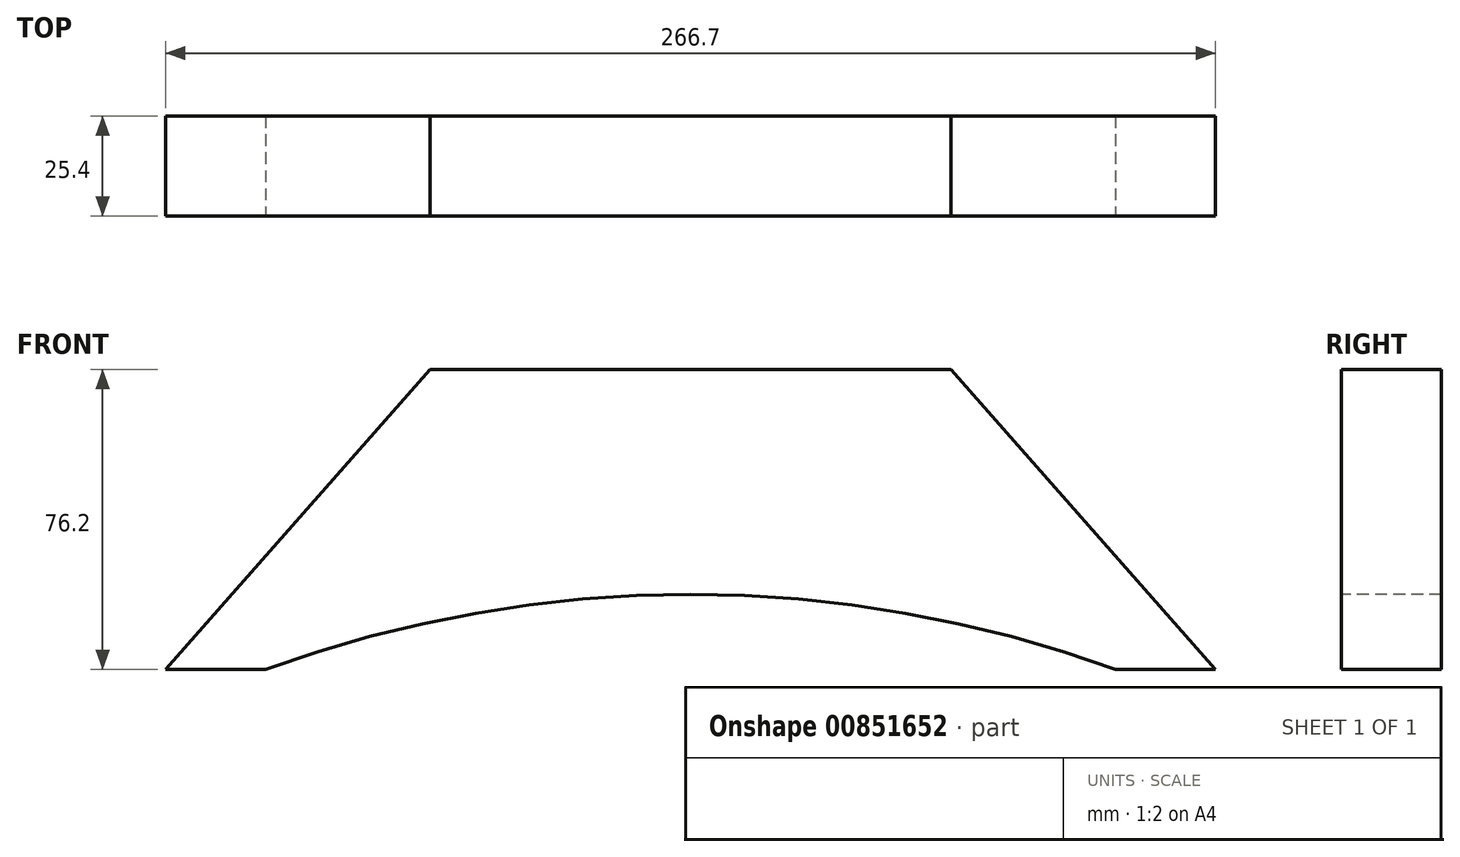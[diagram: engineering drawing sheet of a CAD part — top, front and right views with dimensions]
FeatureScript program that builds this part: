
annotation { "Feature Type Name" : "Feature", "Feature Type Description" : "" }
export const myFeature = defineFeature(function(context is Context, id is Id, definition is map)
    precondition{}
    {
        {
            var Q0;
            Q0=qCreatedBy(makeId("Front.planeOp"),FACE);
            var sketch = newSketch(context, id + "F0", { "sketchPlane" : qUnion([Q0])});
            skLineSegment(sketch, "E0", {"start": v(-134.22, 61.36) * mm, "end": v(183.28, 61.36) * mm});
            skLineSegment(sketch, "E1", {"start": v(-134.22, 61.36) * mm, "end": v(-134.22, -14.84) * mm});
            skLineSegment(sketch, "E2", {"start": v(-134.22, -14.84) * mm, "end": v(183.28, -14.84) * mm});
            skLineSegment(sketch, "E3", {"start": v(183.28, -14.84) * mm, "end": v(183.28, 61.36) * mm});
            skSolve(sketch);
        }
        {
            var Q0;
            Q0 = qSketchRegion(id + "F0", true);
            extrude(context, id + "F1", {"entities" : qUnion([Q0]), "depth" : 25.4 * mm, "offsetDistance" : 25.4 * mm});
        }
        {
            var Q0;
            Q0=makeQuery(id+"F1.opExtrude","CAP_FACE",FACE,{"disambiguationData":[OSD([sQuery(id+"F0.wireOp",EDGE,"E0"),sQuery(id+"F0.wireOp",EDGE,"E1"),sQuery(id+"F0.wireOp",EDGE,"E2"),sQuery(id+"F0.wireOp",EDGE,"E3")])],"isStart":false});
            var sketch = newSketch(context, id + "F2", { "sketchPlane" : qUnion([Q0])});
            skLineSegment(sketch, "E4", {"start": v(-108.82, -14.84) * mm, "end": v(-41.62, 61.36) * mm});
            skLineSegment(sketch, "E5", {"start": v(157.88, -14.84) * mm, "end": v(90.68, 61.36) * mm});
            skSolve(sketch);
        }
        {
            var Q0;
            Q0 = qSketchRegion(id + "F2", true);
            var Q1;
            {var subQ0=sQuery(id+"F2.wireOp",EDGE,"E4");Q1=makeQuery(id+"F2.imprint","IMPRINT",FACE,{"disambiguationData":[TD([[makeQuery(id+"F2.imprint","IMPRINT",EDGE,{"derivedFrom":subQ0}),1.0]])]});}
            var Q2;
            {var subQ0=sQuery(id+"F2.wireOp",EDGE,"E5");Q2=makeQuery(id+"F2.imprint","IMPRINT",FACE,{"disambiguationData":[TD([[makeQuery(id+"F2.imprint","IMPRINT",EDGE,{"derivedFrom":subQ0}),-1.0]])]});}
            extrude(context, id + "F3", {"entities" : qUnion([Q0, Q1, Q2]), "operationType" : NewBodyOperationType.REMOVE, "oppositeDirection" : true, "depth" : 50.8 * mm, "offsetDistance" : 25.4 * mm});
        }
        {
            var Q0;
            Q0=makeQuery(id+"F1.opExtrude","CAP_FACE",FACE,{"disambiguationData":[OSD([sQuery(id+"F0.wireOp",EDGE,"E0"),sQuery(id+"F0.wireOp",EDGE,"E1"),sQuery(id+"F0.wireOp",EDGE,"E2"),sQuery(id+"F0.wireOp",EDGE,"E3")])],"isStart":false});
            var sketch = newSketch(context, id + "F4", { "sketchPlane" : qUnion([Q0])});
            skArc(sketch, "E6", {"start": v(132.48, -14.84) * mm, "mid": v(24.53, 4.2) * mm, "end": v(-83.42, -14.84) * mm});
            skLineSegment(sketch, "E7", {"start": v(-83.42, -14.84) * mm, "end": v(132.48, -14.84) * mm});
            skSolve(sketch);
        }
        {
            var Q0;
            Q0=makeQuery(id+"F4.imprint","IMPRINT",FACE,{"disambiguationData":[TD([[makeQuery(id+"F4.imprint","IMPRINT",EDGE,{"derivedFrom":sQuery(id+"F4.wireOp",EDGE,"E6")}),1.0]])]});
            extrude(context, id + "F5", {"entities" : qUnion([Q0]), "operationType" : NewBodyOperationType.REMOVE, "oppositeDirection" : true, "depth" : 508 * mm, "offsetDistance" : 25.4 * mm});
        }
    });
